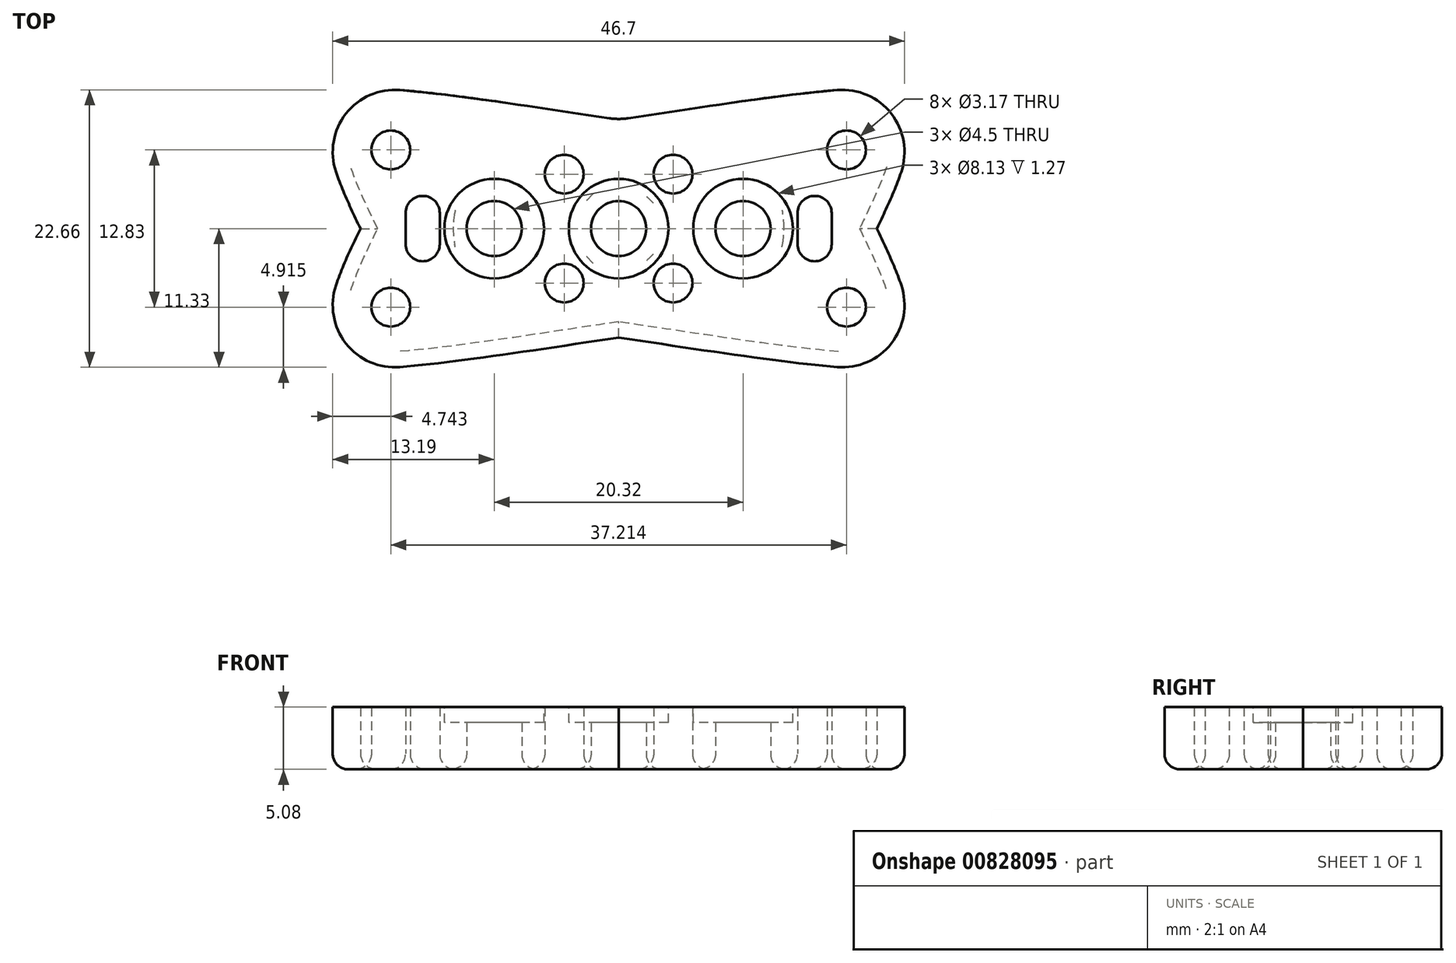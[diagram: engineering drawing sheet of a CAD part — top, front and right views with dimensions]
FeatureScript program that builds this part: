
annotation { "Feature Type Name" : "Feature", "Feature Type Description" : "" }
export const myFeature = defineFeature(function(context is Context, id is Id, definition is map)
    precondition{}
    {
        {
            var Q0;
            Q0=qCreatedBy(makeId("Top.planeOp"),FACE);
            var sketch = newSketch(context, id + "F0", { "sketchPlane" : qUnion([Q0])});
            skLineSegment(sketch, "E0.bottom", {"start": v(-21.08, -8.9) * mm, "end": v(21.08, -8.9) * mm, "construction": true});
            skLineSegment(sketch, "E0.top", {"start": v(-21.08, 8.9) * mm, "end": v(21.08, 8.9) * mm, "construction": true});
            skLineSegment(sketch, "E0.left", {"start": v(-21.08, -8.89) * mm, "end": v(-21.08, 8.89) * mm, "construction": true});
            skLineSegment(sketch, "E0.right", {"start": v(21.08, -8.89) * mm, "end": v(21.08, 8.89) * mm, "construction": true});
            skCircle(sketch, "E1", {"center": v(-10.16, 0) * mm, "radius": 2.25 * mm});
            skCircle(sketch, "E2", {"center": v(10.16, 0) * mm, "radius": 2.25 * mm});
            skCircle(sketch, "E3", {"center": v(0, 0) * mm, "radius": 2.25 * mm});
            skLineSegment(sketch, "E4.bottom", {"start": v(-17.4, 1.27) * mm, "end": v(-14.6, 1.27) * mm, "construction": true});
            skLineSegment(sketch, "E4.top", {"start": v(-17.4, -1.27) * mm, "end": v(-14.6, -1.27) * mm, "construction": true});
            skLineSegment(sketch, "E4.left", {"start": v(-17.4, 1.27) * mm, "end": v(-17.4, -1.27) * mm});
            skLineSegment(sketch, "E4.right", {"start": v(-14.6, 1.27) * mm, "end": v(-14.6, -1.27) * mm});
            skLineSegment(sketch, "E5.bottom", {"start": v(14.6, 1.27) * mm, "end": v(17.4, 1.27) * mm, "construction": true});
            skLineSegment(sketch, "E5.top", {"start": v(14.6, -1.27) * mm, "end": v(17.4, -1.27) * mm, "construction": true});
            skLineSegment(sketch, "E5.left", {"start": v(14.6, 1.27) * mm, "end": v(14.6, -1.27) * mm});
            skLineSegment(sketch, "E5.right", {"start": v(17.4, 1.27) * mm, "end": v(17.4, -1.27) * mm});
            skArc(sketch, "E6", {"start": v(-17.4, -1.27) * mm, "mid": v(-16, -2.67) * mm, "end": v(-14.6, -1.27) * mm});
            skArc(sketch, "E7", {"start": v(-14.6, 1.27) * mm, "mid": v(-16, 2.67) * mm, "end": v(-17.4, 1.27) * mm});
            skArc(sketch, "E8", {"start": v(17.4, 1.27) * mm, "mid": v(16, 2.67) * mm, "end": v(14.6, 1.27) * mm});
            skArc(sketch, "E9", {"start": v(14.6, -1.27) * mm, "mid": v(16, -2.67) * mm, "end": v(17.4, -1.27) * mm});
            skCircle(sketch, "E10", {"center": v(-4.45, 4.45) * mm, "radius": 1.59 * mm});
            skLineSegment(sketch, "E11", {"start": v(-4.45, 4.45) * mm, "end": v(-4.45, 0) * mm, "construction": true});
            skLineSegment(sketch, "E12", {"start": v(-4.45, 0) * mm, "end": v(0, 0) * mm, "construction": true});
            skCircle(sketch, "E13.1.0", {"center": v(-4.45, -4.45) * mm, "radius": 1.59 * mm});
            skCircle(sketch, "E13.2.0", {"center": v(4.45, -4.45) * mm, "radius": 1.59 * mm});
            skCircle(sketch, "E13.3.0", {"center": v(4.45, 4.45) * mm, "radius": 1.59 * mm});
            skCircle(sketch, "E14", {"center": v(-21.08, 8.9) * mm, "radius": 3.5 * mm, "construction": true});
            skLineSegment(sketch, "E15", {"start": v(-21.08, 8.89) * mm, "end": v(-23.56, 11.37) * mm, "construction": true});
            skFitSpline(sketch, "E16", {"points": [v(-23.56, 11.37) * mm, v(-23.56, 6.41) * mm, v(-21.08, 0) * mm], "startDerivative": vector(-1.05, -10.54) * mm, "endDerivative": vector(5.81, -12.15) * mm});
            skFitSpline(sketch, "E17", {"points": [v(-23.56, 11.37) * mm, v(-18.6, 11.37) * mm, v(0, 8.9) * mm], "startDerivative": vector(12.29, 0.64) * mm, "endDerivative": vector(32.65, -4.98) * mm});
            skFitSpline(sketch, "E18.MirrorCS", {"points": [v(-23.56, -11.37) * mm, v(-23.56, -6.41) * mm, v(-21.08, 0) * mm], "startDerivative": vector(-1.05, 10.54) * mm, "endDerivative": vector(5.81, 12.15) * mm});
            skFitSpline(sketch, "E19.MirrorCS", {"points": [v(-23.56, -11.37) * mm, v(-18.6, -11.37) * mm, v(0, -8.9) * mm], "startDerivative": vector(12.29, -0.64) * mm, "endDerivative": vector(32.65, 4.98) * mm});
            skFitSpline(sketch, "E20.MirrorCS", {"points": [v(-23.56, 11.37) * mm, v(-23.56, 6.41) * mm, v(-21.08, 0) * mm], "startDerivative": vector(-1.05, -10.54) * mm, "endDerivative": vector(5.81, -12.15) * mm});
            skFitSpline(sketch, "E21.MirrorCS", {"points": [v(23.56, 11.37) * mm, v(18.6, 11.37) * mm, v(0, 8.9) * mm], "startDerivative": vector(-12.29, 0.64) * mm, "endDerivative": vector(-32.65, -4.98) * mm});
            skFitSpline(sketch, "E22.MirrorCS", {"points": [v(23.56, 11.37) * mm, v(23.56, 6.41) * mm, v(21.08, 0) * mm], "startDerivative": vector(1.05, -10.54) * mm, "endDerivative": vector(-5.81, -12.15) * mm});
            skFitSpline(sketch, "E23.MirrorCS", {"points": [v(23.56, -11.37) * mm, v(18.6, -11.37) * mm, v(0, -8.9) * mm], "startDerivative": vector(-12.29, -0.64) * mm, "endDerivative": vector(-32.65, 4.98) * mm});
            skFitSpline(sketch, "E24.MirrorCS", {"points": [v(23.56, -11.37) * mm, v(23.56, -6.41) * mm, v(21.08, 0) * mm], "startDerivative": vector(1.05, 10.54) * mm, "endDerivative": vector(-5.81, 12.15) * mm});
            skLineSegment(sketch, "E25", {"start": v(-21.08, 8.9) * mm, "end": v(-18.6, 6.41) * mm, "construction": true});
            skCircle(sketch, "E26", {"center": v(-18.6, 6.41) * mm, "radius": 1.59 * mm});
            skCircle(sketch, "E27", {"center": v(-18.6, -6.41) * mm, "radius": 1.59 * mm});
            skCircle(sketch, "E28", {"center": v(18.6, 6.41) * mm, "radius": 1.59 * mm});
            skCircle(sketch, "E29", {"center": v(18.6, -6.41) * mm, "radius": 1.59 * mm});
            skSolve(sketch);
        }
        {
            var Q0;
            Q0 = qSketchRegion(id + "F0", true);
            extrude(context, id + "F1", {"entities" : qUnion([Q0]), "depth" : 5.08 * mm, "offsetDistance" : 25.4 * mm});
        }
        {
            var Q0;
            Q0=makeQuery(id+"F1.opExtrude","CAP_FACE",FACE,{"disambiguationData":[OSD([sQuery(id+"F0.wireOp",EDGE,"E0.bottom"),sQuery(id+"F0.wireOp",EDGE,"E0.top"),sQuery(id+"F0.wireOp",EDGE,"E0.left"),sQuery(id+"F0.wireOp",EDGE,"E0.right"),sQuery(id+"F0.wireOp",EDGE,"E1"),sQuery(id+"F0.wireOp",EDGE,"E2"),sQuery(id+"F0.wireOp",EDGE,"E3"),sQuery(id+"F0.wireOp",EDGE,"E4.left"),sQuery(id+"F0.wireOp",EDGE,"E4.right"),sQuery(id+"F0.wireOp",EDGE,"E5.left"),sQuery(id+"F0.wireOp",EDGE,"E5.right"),sQuery(id+"F0.wireOp",EDGE,"E6"),sQuery(id+"F0.wireOp",EDGE,"E7"),sQuery(id+"F0.wireOp",EDGE,"E8"),sQuery(id+"F0.wireOp",EDGE,"E9"),sQuery(id+"F0.wireOp",EDGE,"E10"),sQuery(id+"F0.wireOp",EDGE,"E13.1.0"),sQuery(id+"F0.wireOp",EDGE,"E13.2.0"),sQuery(id+"F0.wireOp",EDGE,"E13.3.0")])],"isStart":false});
            var sketch = newSketch(context, id + "F2", { "sketchPlane" : qUnion([Q0])});
            skCircle(sketch, "E30", {"center": v(-10.16, 0) * mm, "radius": 4.06 * mm});
            skCircle(sketch, "E31", {"center": v(0, 0) * mm, "radius": 4.06 * mm});
            skCircle(sketch, "E32", {"center": v(10.16, 0) * mm, "radius": 4.06 * mm});
            skSolve(sketch);
        }
        {
            var Q0;
            Q0=makeQuery(id+"F1.opExtrude","SWEPT_EDGE",EDGE,{"disambiguationData":[OSD([sQuery(id+"F0.wireOp",EDGE,"E17"),sQuery(id+"F0.wireOp",EDGE,"E20.MirrorCS")])]});
            var Q1;
            Q1=makeQuery(id+"F1.opExtrude","SWEPT_EDGE",EDGE,{"disambiguationData":[OSD([sQuery(id+"F0.wireOp",EDGE,"E18.MirrorCS"),sQuery(id+"F0.wireOp",EDGE,"E19.MirrorCS")])]});
            var Q2;
            Q2=makeQuery(id+"F1.opExtrude","SWEPT_EDGE",EDGE,{"disambiguationData":[OSD([sQuery(id+"F0.wireOp",EDGE,"E21.MirrorCS"),sQuery(id+"F0.wireOp",EDGE,"E22.MirrorCS")])]});
            var Q3;
            Q3=makeQuery(id+"F1.opExtrude","SWEPT_EDGE",EDGE,{"disambiguationData":[OSD([sQuery(id+"F0.wireOp",EDGE,"E23.MirrorCS"),sQuery(id+"F0.wireOp",EDGE,"E24.MirrorCS")])]});
            fillet(context, id + "F3", {"entities" : qUnion([Q0, Q1, Q2, Q3]), "radius" : 5.08 * mm, "tangentPropagation" : true, "allowEdgeOverflow" : false});
        }
        {
            var Q0;
            Q0=makeQuery(id+"F1.opExtrude","CAP_FACE",FACE,{"disambiguationData":[OSD([sQuery(id+"F0.wireOp",EDGE,"E0.bottom"),sQuery(id+"F0.wireOp",EDGE,"E0.top"),sQuery(id+"F0.wireOp",EDGE,"E0.left"),sQuery(id+"F0.wireOp",EDGE,"E0.right"),sQuery(id+"F0.wireOp",EDGE,"E1"),sQuery(id+"F0.wireOp",EDGE,"E2"),sQuery(id+"F0.wireOp",EDGE,"E3"),sQuery(id+"F0.wireOp",EDGE,"E4.left"),sQuery(id+"F0.wireOp",EDGE,"E4.right"),sQuery(id+"F0.wireOp",EDGE,"E5.left"),sQuery(id+"F0.wireOp",EDGE,"E5.right"),sQuery(id+"F0.wireOp",EDGE,"E6"),sQuery(id+"F0.wireOp",EDGE,"E7"),sQuery(id+"F0.wireOp",EDGE,"E8"),sQuery(id+"F0.wireOp",EDGE,"E9"),sQuery(id+"F0.wireOp",EDGE,"E10"),sQuery(id+"F0.wireOp",EDGE,"E13.1.0"),sQuery(id+"F0.wireOp",EDGE,"E13.2.0"),sQuery(id+"F0.wireOp",EDGE,"E13.3.0")])],"isStart":true});
            fillet(context, id + "F4", {"entities" : qUnion([Q0]), "radius" : 1.27 * mm, "tangentPropagation" : true, "allowEdgeOverflow" : false});
        }
        {
            var Q0;
            Q0 = qSketchRegion(id + "F2", true);
            extrude(context, id + "F5", {"entities" : qUnion([Q0]), "operationType" : NewBodyOperationType.REMOVE, "oppositeDirection" : true, "depth" : 1.27 * mm, "offsetDistance" : 25.4 * mm});
        }
    });
